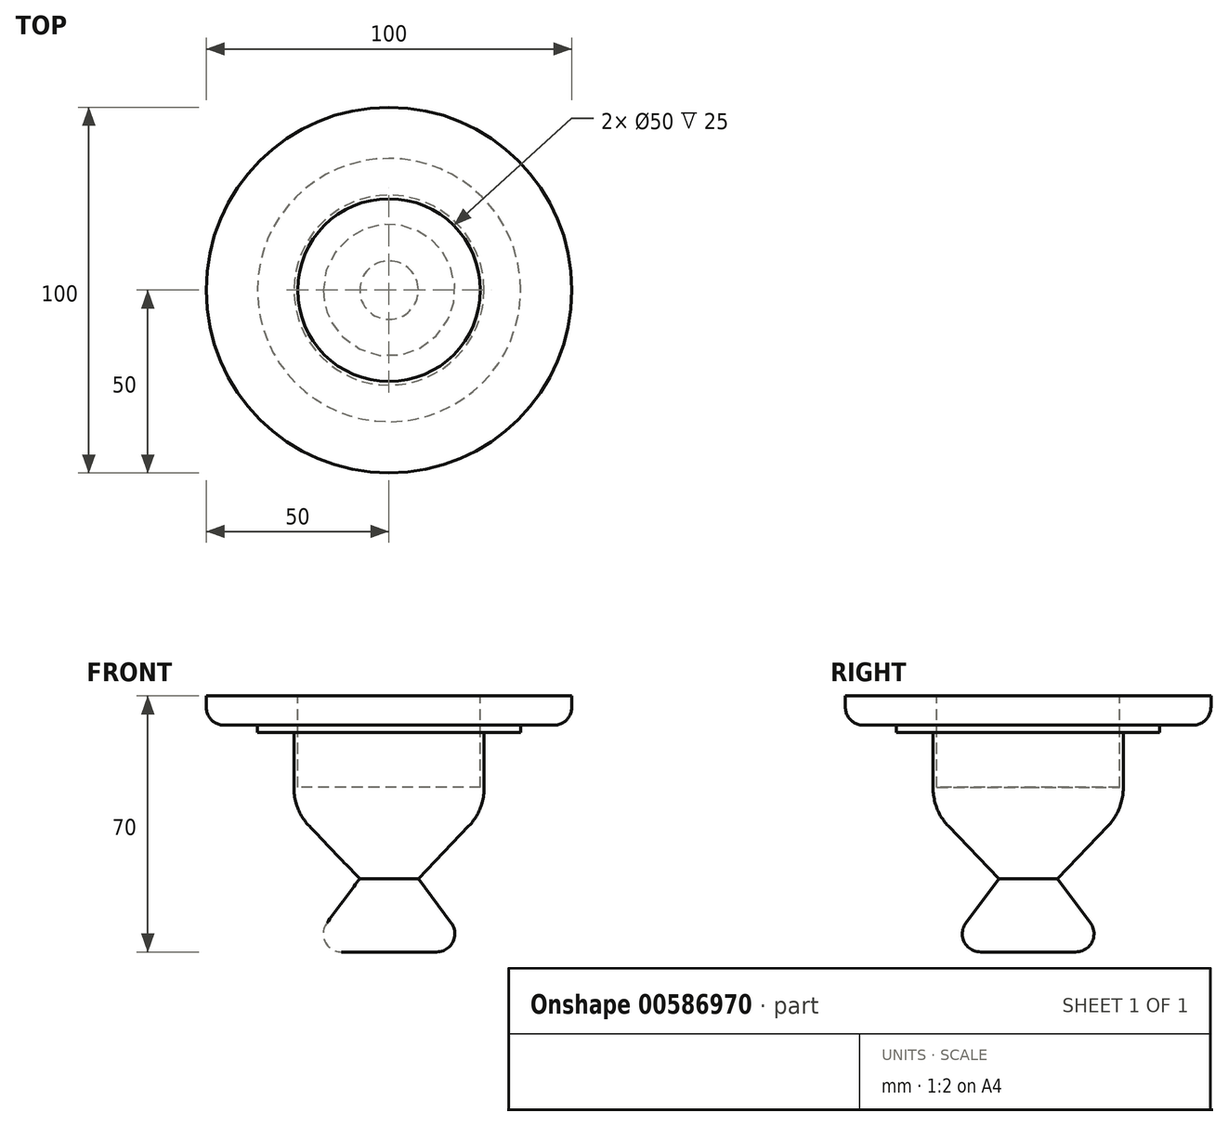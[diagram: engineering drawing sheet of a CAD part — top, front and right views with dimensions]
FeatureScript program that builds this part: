
annotation { "Feature Type Name" : "Feature", "Feature Type Description" : "" }
export const myFeature = defineFeature(function(context is Context, id is Id, definition is map)
    precondition{}
    {
        {
            var Q0;
            Q0=qCreatedBy(makeId("Front.planeOp"),FACE);
            var sketch = newSketch(context, id + "F0", { "sketchPlane" : qUnion([Q0])});
            skLineSegment(sketch, "E0", {"start": v(0, 0) * mm, "end": v(0, 70) * mm, "construction": true});
            skLineSegment(sketch, "E1", {"start": v(0, 70) * mm, "end": v(50, 70) * mm});
            skLineSegment(sketch, "E2", {"start": v(50, 70) * mm, "end": v(50, 67) * mm});
            skLineSegment(sketch, "E3", {"start": v(45, 62) * mm, "end": v(36, 62) * mm});
            skLineSegment(sketch, "E4", {"start": v(36, 62) * mm, "end": v(36, 60) * mm});
            skLineSegment(sketch, "E5", {"start": v(36, 60) * mm, "end": v(26, 60) * mm});
            skLineSegment(sketch, "E6", {"start": v(26, 60) * mm, "end": v(26, 44.82) * mm});
            skLineSegment(sketch, "E7", {"start": v(21.83, 34.44) * mm, "end": v(8, 20) * mm});
            skLineSegment(sketch, "E8", {"start": v(8, 20) * mm, "end": v(17, 8) * mm});
            skLineSegment(sketch, "E9", {"start": v(13, 0) * mm, "end": v(0, 0) * mm});
            skPoint(sketch, "E10.visualSharp", {"position": v(50, 62) * mm});
            skArc(sketch, "E10.filletArc", {"start": v(45, 62) * mm, "mid": v(48.54, 63.46) * mm, "end": v(50, 67) * mm});
            skPoint(sketch, "E11.visualSharp", {"position": v(26, 38.8) * mm});
            skArc(sketch, "E11.filletArc", {"start": v(21.83, 34.44) * mm, "mid": v(24.92, 39.23) * mm, "end": v(26, 44.82) * mm});
            skPoint(sketch, "E12.visualSharp", {"position": v(23, 0) * mm});
            skArc(sketch, "E12.filletArc", {"start": v(13, 0) * mm, "mid": v(17.47, 2.76) * mm, "end": v(17, 8) * mm});
            skLineSegment(sketch, "E13", {"start": v(0, 0) * mm, "end": v(0, 70) * mm});
            skSolve(sketch);
        }
        {
            var Q0;
            Q0 = qSketchRegion(id + "F0", true);
            var Q1;
            Q1=sQuery(id+"F0.wireOp",EDGE,"E13");
            revolve(context, id + "F1", {"entities" : qUnion([Q0]), "axis" : qUnion([Q1]), "revolveType" : RevolveType.FULL});
        }
        {
            var Q0;
            Q0=makeQuery(id+"F1.opRevolve","SWEPT_FACE",FACE,{"disambiguationData":[OSD([sQuery(id+"F0.wireOp",EDGE,"E1")])]});
            var sketch = newSketch(context, id + "F2", { "sketchPlane" : qUnion([Q0])});
            skCircle(sketch, "E14", {"center": v(0, 0) * mm, "radius": 25 * mm});
            skSolve(sketch);
        }
        {
            var Q0;
            Q0 = qSketchRegion(id + "F2", true);
            extrude(context, id + "F3", {"entities" : qUnion([Q0]), "operationType" : NewBodyOperationType.REMOVE, "oppositeDirection" : true, "depth" : 25 * mm, "offsetDistance" : 25 * mm});
        }
    });
